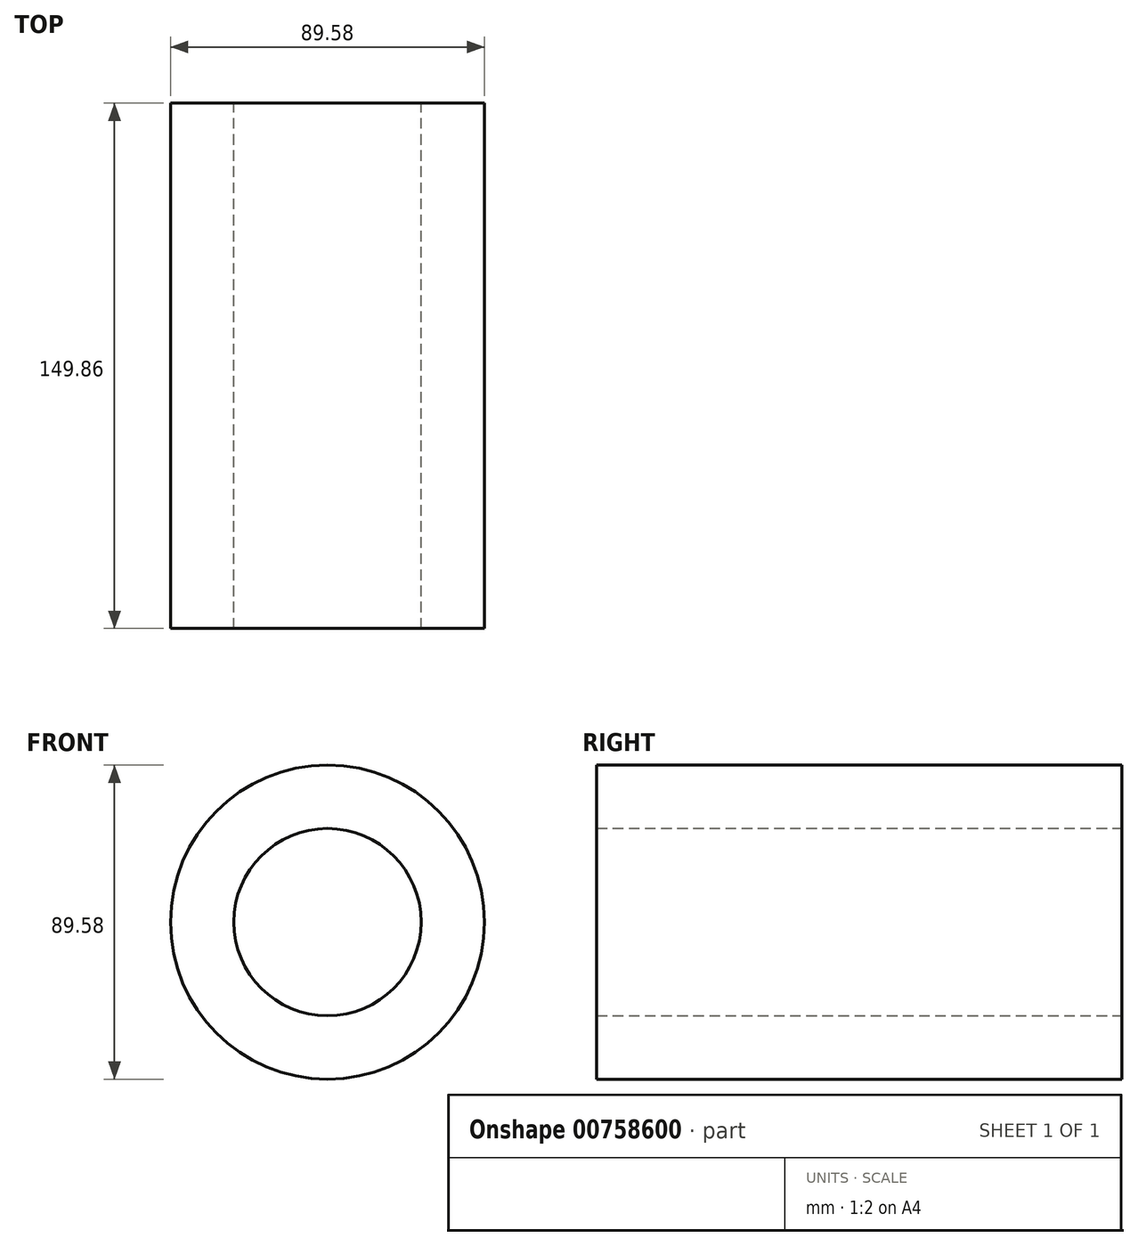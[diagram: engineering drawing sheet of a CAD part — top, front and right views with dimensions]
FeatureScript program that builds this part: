
annotation { "Feature Type Name" : "Feature", "Feature Type Description" : "" }
export const myFeature = defineFeature(function(context is Context, id is Id, definition is map)
    precondition{}
    {
        {
            var Q0;
            Q0=qCreatedBy(makeId("Front.planeOp"),FACE);
            var sketch = newSketch(context, id + "F0", { "sketchPlane" : qUnion([Q0])});
            skCircle(sketch, "E0", {"center": v(0, 0) * mm, "radius": 44.8 * mm});
            skCircle(sketch, "E1", {"center": v(0, 0) * mm, "radius": 26.73 * mm});
            skSolve(sketch);
        }
        {
            var Q0;
            Q0=makeQuery(id+"F0.imprint","IMPRINT",FACE,{"disambiguationData":[TD([[makeQuery(id+"F0.imprint","IMPRINT",EDGE,{"derivedFrom":sQuery(id+"F0.wireOp",EDGE,"E0")}),1.0]])]});
            extrude(context, id + "F1", {"entities" : qUnion([Q0]), "depth" : 149.86 * mm, "offsetDistance" : 25.4 * mm});
        }
    });
